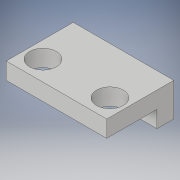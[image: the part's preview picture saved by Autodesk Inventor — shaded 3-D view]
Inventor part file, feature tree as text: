
AUTODESK INVENTOR PART (.ipt)
format: ipt  version: 2017 (Build 210142000, 142)  size: 110,592 bytes
history: native  units: in
note: dims shown in document units (in); Inventor stores cm internally (conversion verified against a paired STEP export)
features: sketch x2, extrude x1, hole x1, projected_geometry x1
ambient origin geometry x8: Origin, YZ Plane, XZ Plane, XY Plane, X Axis, Y Axis, Z Axis, Center Point
bodies: Solid1 (feature_tree)
feature tree (5):
  extrude  "Extrusion1"  Depth=1.0in
  hole  "Hole1"  [1 undecoded]
  sketch  "Sketch1"  dims[d0=0.5in d1=1.0in]
  sketch  "Sketch2"  dims[d2=0.25in d3=0.25in d4=1.5in d5=0.0in d6=1.5in d7=0.25in d8=0.25in d9=0.4in d10=0.625in d11=0.375in d12=0.25in d13=0.5635in d14=0.903in d15=0.8108in]
  projected_geometry  "Projected Loop1"
note: 1 required parameter value undecoded (feature->parameter linkage not recoverable at this tier; creation-order binding heuristic only, values carry confidence <= 0.55)
